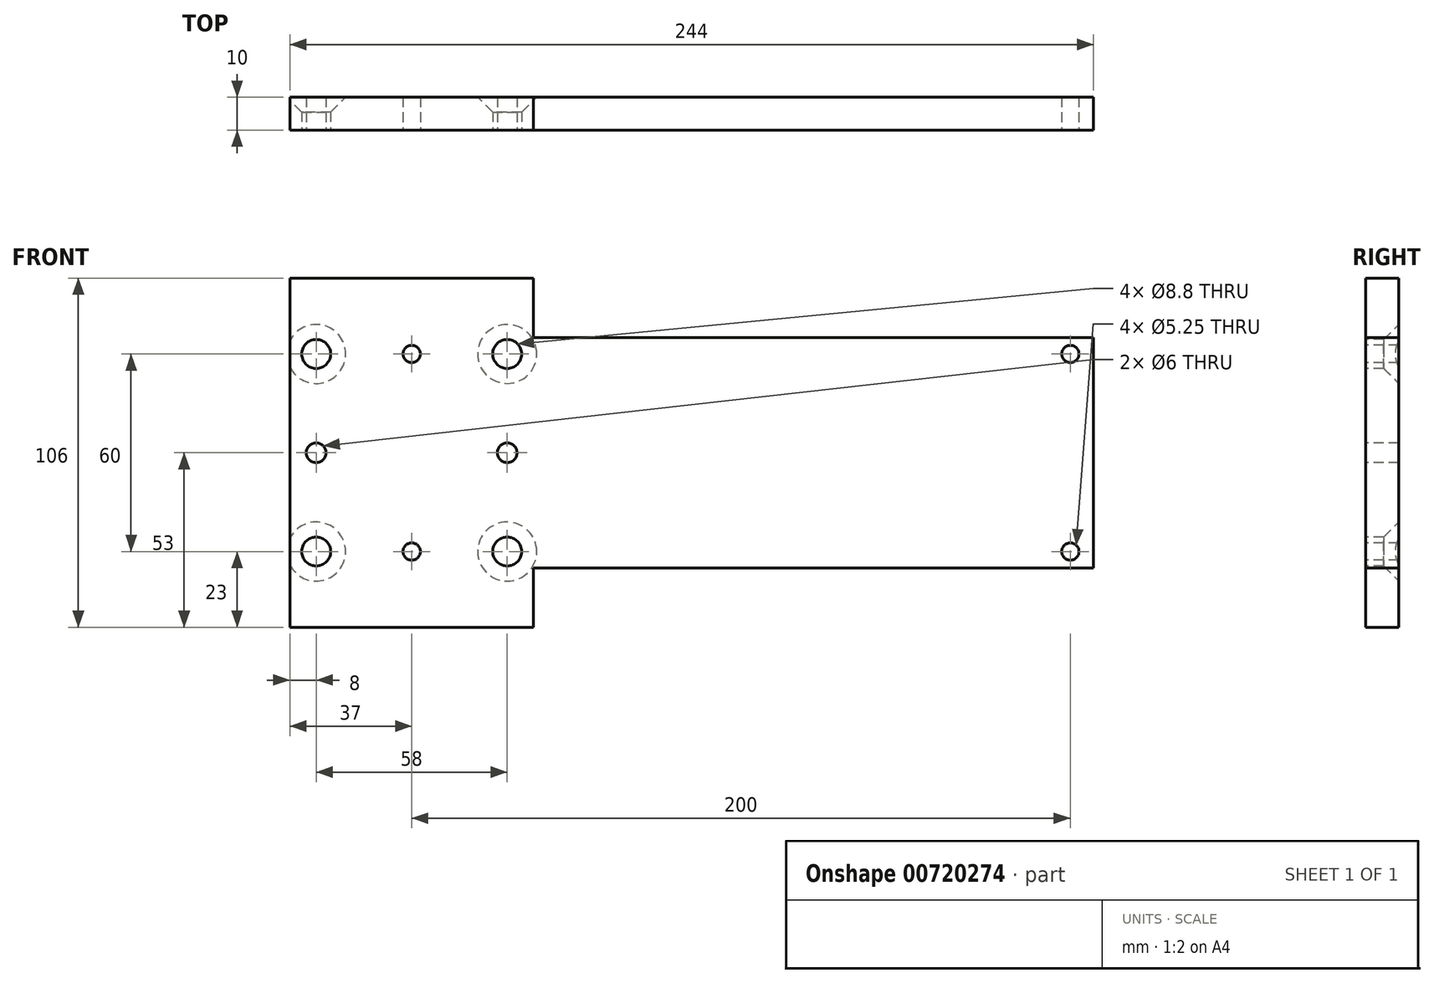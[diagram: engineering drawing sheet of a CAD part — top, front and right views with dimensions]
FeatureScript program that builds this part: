
annotation { "Feature Type Name" : "Feature", "Feature Type Description" : "" }
export const myFeature = defineFeature(function(context is Context, id is Id, definition is map)
    precondition{}
    {
        {
            var Q0;
            Q0=qCreatedBy(makeId("Front.planeOp"),FACE);
            var sketch = newSketch(context, id + "F0", { "sketchPlane" : qUnion([Q0])});
            skLineSegment(sketch, "E0.bottom", {"start": v(37, 53) * mm, "end": v(-37, 53) * mm});
            skLineSegment(sketch, "E0.top", {"start": v(37, -53) * mm, "end": v(-37, -53) * mm});
            skLineSegment(sketch, "E0.left", {"start": v(37, 53) * mm, "end": v(37, -53) * mm});
            skLineSegment(sketch, "E0.right", {"start": v(-37, 53) * mm, "end": v(-37, -53) * mm});
            skPoint(sketch, "E0.middle", {"position": v(0, 0) * mm});
            skPoint(sketch, "E1", {"position": v(-29, 0) * mm});
            skPoint(sketch, "E2", {"position": v(-29, 30) * mm});
            skPoint(sketch, "E3", {"position": v(29, 30) * mm});
            skPoint(sketch, "E4", {"position": v(29, 0) * mm});
            skPoint(sketch, "E5", {"position": v(29, -30) * mm});
            skPoint(sketch, "E6", {"position": v(-29, -30) * mm});
            skLineSegment(sketch, "E7.bottom", {"start": v(37, 0) * mm, "end": v(207, 0) * mm});
            skLineSegment(sketch, "E7.top", {"start": v(37, 35) * mm, "end": v(207, 35) * mm});
            skLineSegment(sketch, "E7.left", {"start": v(37, 0) * mm, "end": v(37, 35) * mm});
            skLineSegment(sketch, "E7.right", {"start": v(207, 0) * mm, "end": v(207, 35) * mm});
            skLineSegment(sketch, "E8.top", {"start": v(37, -35) * mm, "end": v(207, -35) * mm});
            skLineSegment(sketch, "E8.left", {"start": v(37, 0) * mm, "end": v(37, -35) * mm});
            skLineSegment(sketch, "E8.right", {"start": v(207, 0) * mm, "end": v(207, -35) * mm});
            skSolve(sketch);
        }
        {
            var Q0;
            Q0=makeQuery(id+"F0.imprint","IMPRINT",FACE,{"disambiguationData":[TD([[makeQuery(id+"F0.imprint","IMPRINT",EDGE,{"derivedFrom":sQuery(id+"F0.wireOp",EDGE,"E0.bottom")}),1.0]])]});
            var Q1;
            Q1=makeQuery(id+"F0.imprint","IMPRINT",FACE,{"disambiguationData":[TD([[makeQuery(id+"F0.imprint","IMPRINT",EDGE,{"derivedFrom":sQuery(id+"F0.wireOp",EDGE,"E7.bottom")}),-1.0]])]});
            var Q2;
            Q2=makeQuery(id+"F0.imprint","IMPRINT",FACE,{"disambiguationData":[TD([[makeQuery(id+"F0.imprint","IMPRINT",EDGE,{"derivedFrom":sQuery(id+"F0.wireOp",EDGE,"E7.top")}),-1.0]])]});
            extrude(context, id + "F1", {"entities" : qUnion([Q0, Q1, Q2]), "depth" : 10 * mm, "offsetDistance" : 25 * mm});
        }
        {
            var Q0;
            Q0=sQuery(id+"F0.wireOp",VERTEX,"E1");
            var Q1;
            Q1=sQuery(id+"F0.wireOp",VERTEX,"E4");
            var Q2;
            Q2=makeQuery(id+"F1.opExtrude","SWEPT_BODY",BODY,{"disambiguationData":[OSD([sQuery(id+"F0.wireOp",EDGE,"E0.bottom"),sQuery(id+"F0.wireOp",EDGE,"E0.top"),sQuery(id+"F0.wireOp",EDGE,"E0.left"),sQuery(id+"F0.wireOp",EDGE,"E0.right")])]});
            hole(context, id + "F2", {"style" : HoleStyle.SIMPLE, "endStyle" : HoleEndStyle.BLIND, "oppositeDirection" : true, "holeDiameter" : 6 * mm, "majorDiameter" : 5 * mm, "holeDepth" : 40 * mm, "tappedDepth" : 12 * mm, "tapClearance" : 3, "locations" : qUnion([Q0, Q1]), "scope" : qUnion([Q2])});
        }
        {
            var Q0;
            Q0=sQuery(id+"F0.wireOp",VERTEX,"E5");
            var Q1;
            Q1=sQuery(id+"F0.wireOp",VERTEX,"E6");
            var Q2;
            Q2=sQuery(id+"F0.wireOp",VERTEX,"E3");
            var Q3;
            Q3=sQuery(id+"F0.wireOp",VERTEX,"E2");
            var Q4;
            Q4=makeQuery(id+"F1.opExtrude","SWEPT_BODY",BODY,{"disambiguationData":[OSD([sQuery(id+"F0.wireOp",EDGE,"E0.bottom"),sQuery(id+"F0.wireOp",EDGE,"E0.top"),sQuery(id+"F0.wireOp",EDGE,"E0.left"),sQuery(id+"F0.wireOp",EDGE,"E0.right")])]});
            hole(context, id + "F3", {"style" : HoleStyle.C_SINK, "endStyle" : HoleEndStyle.BLIND, "oppositeDirection" : true, "standardTappedOrClearance" : lookupTablePath({ "standard" : "ISO", "fit" : "Normal", "size" : "M8", "type" : "Clearance" }), "standardBlindInLast" : lookupTablePath({ "fit" : "Standard", "standard" : "ISO", "size" : "M8", "type" : "Clearance" }), "holeDiameter" : 8.8 * mm, "cSinkDiameter" : 17.92 * mm, "cSinkAngle" : 90 * degree, "majorDiameter" : 5 * mm, "holeDepth" : 40 * mm, "tappedDepth" : 12 * mm, "tapClearance" : 3, "locations" : qUnion([Q0, Q1, Q2, Q3]), "scope" : qUnion([Q4])});
        }
        {
            var Q0;
            Q0=makeQuery(id+"F0.imprint","IMPRINT",FACE,{"disambiguationData":[TD([[makeQuery(id+"F0.imprint","IMPRINT",EDGE,{"derivedFrom":sQuery(id+"F0.wireOp",EDGE,"E0.bottom")}),1.0]])]});
            var sketch = newSketch(context, id + "F4", { "sketchPlane" : qUnion([Q0])});
            skPoint(sketch, "E9", {"position": v(0, -30) * mm});
            skPoint(sketch, "E10", {"position": v(0, 30) * mm});
            skPoint(sketch, "E11", {"position": v(200, -30) * mm});
            skPoint(sketch, "E12", {"position": v(200, 30) * mm});
            skSolve(sketch);
        }
        {
            var Q0;
            Q0=sQuery(id+"F4.wireOp",VERTEX,"E9");
            var Q1;
            Q1=sQuery(id+"F4.wireOp",VERTEX,"E10");
            var Q2;
            Q2=sQuery(id+"F4.wireOp",VERTEX,"E11");
            var Q3;
            Q3=sQuery(id+"F4.wireOp",VERTEX,"E12");
            var Q4;
            Q4=makeQuery(id+"F1.opExtrude","SWEPT_BODY",BODY,{"disambiguationData":[OSD([sQuery(id+"F0.wireOp",EDGE,"E0.bottom"),sQuery(id+"F0.wireOp",EDGE,"E0.top"),sQuery(id+"F0.wireOp",EDGE,"E0.left"),sQuery(id+"F0.wireOp",EDGE,"E0.right")])]});
            hole(context, id + "F5", {"style" : HoleStyle.SIMPLE, "endStyle" : HoleEndStyle.BLIND, "oppositeDirection" : true, "standardTappedOrClearance" : lookupTablePath({ "standard" : "ISO", "fit" : "Close", "size" : "M5", "type" : "Clearance" }), "standardBlindInLast" : lookupTablePath({ "fit" : "Close", "standard" : "ISO", "size" : "M5", "type" : "Clearance" }), "holeDiameter" : 5.25 * mm, "majorDiameter" : 5 * mm, "holeDepth" : 40 * mm, "tappedDepth" : 12 * mm, "tapClearance" : 3, "locations" : qUnion([Q0, Q1, Q2, Q3]), "scope" : qUnion([Q4])});
        }
    });
